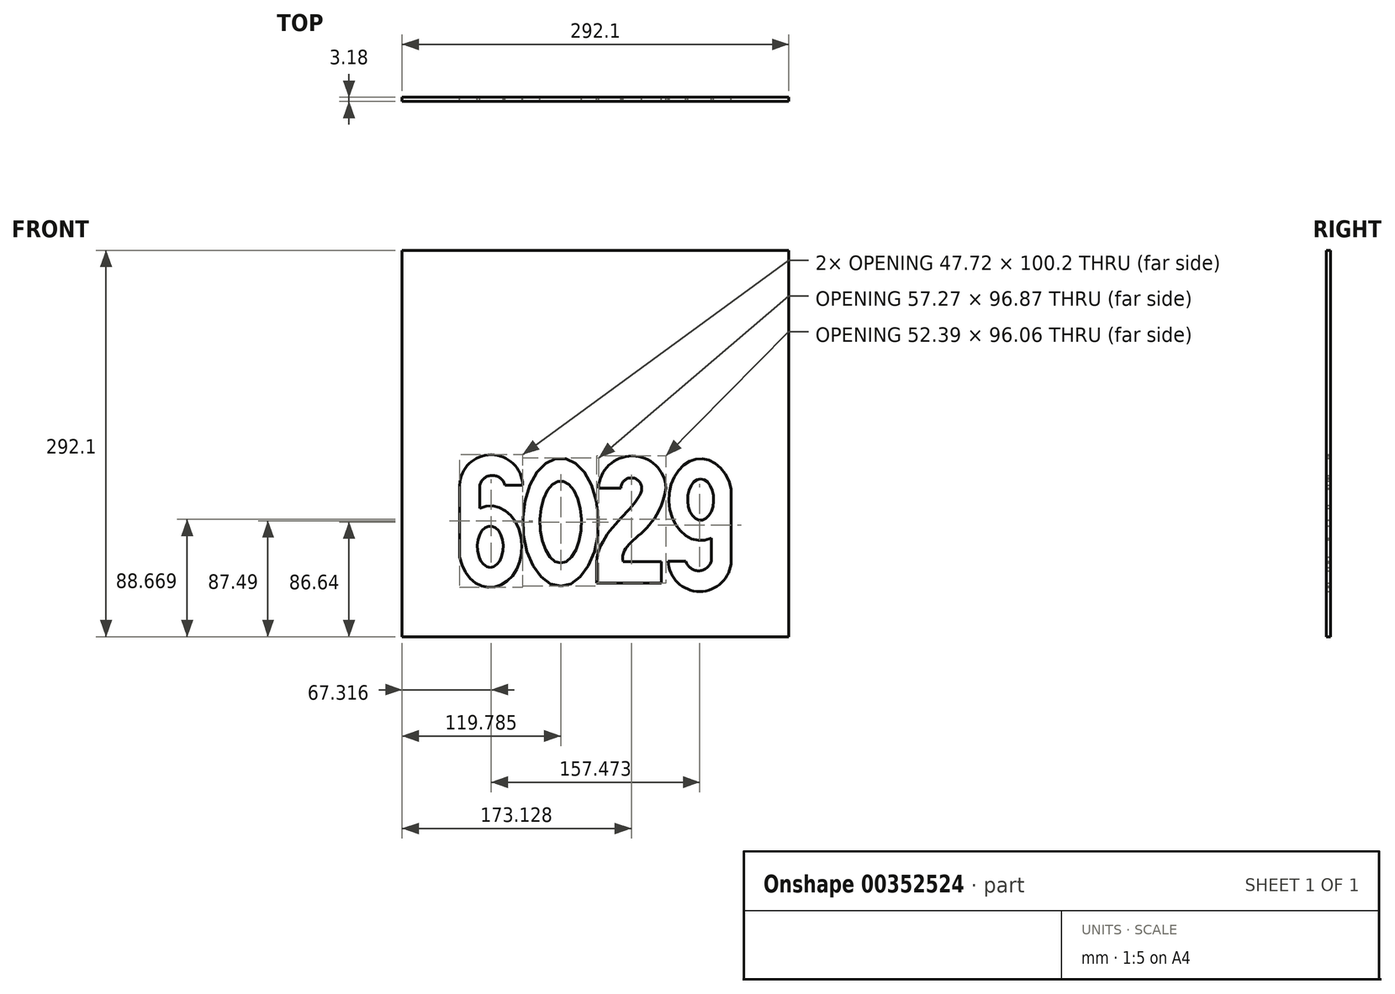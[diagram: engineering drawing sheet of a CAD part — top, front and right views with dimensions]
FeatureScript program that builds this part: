
annotation { "Feature Type Name" : "Feature", "Feature Type Description" : "" }
export const myFeature = defineFeature(function(context is Context, id is Id, definition is map)
    precondition{}
    {
        {
            var Q0;
            Q0=qCreatedBy(makeId("Front.planeOp"),FACE);
            var sketch = newSketch(context, id + "F0", { "sketchPlane" : qUnion([Q0])});
            skLineSegment(sketch, "E0", {"start": v(-95.03, -29.54) * mm, "end": v(-108.48, -29.54) * mm});
            skArc(sketch, "E1", {"start": v(-108.48, -29.54) * mm, "mid": v(-118.05, -22.2) * mm, "end": v(-127.62, -29.54) * mm});
            skArc(sketch, "E2", {"start": v(-95.03, -29.54) * mm, "mid": v(-118.9, -6.52) * mm, "end": v(-142.76, -29.54) * mm});
            skLineSegment(sketch, "E3", {"start": v(-142.76, -29.54) * mm, "end": v(-142.76, -83.99) * mm});
            skLineSegment(sketch, "E4", {"start": v(-127.62, -29.54) * mm, "end": v(-127.62, -46.95) * mm});
            skEllipse(sketch, "E5", {"center": v(-119.6, -76.04) * mm, "majorRadius": 15.63 * mm, "minorRadius": 9.82 * mm, "majorAxis": v(0, -1)});
            skEllipticalArc(sketch, "E6", {});
            skEllipse(sketch, "E7", {"center": v(-66.42, -57.47) * mm, "majorRadius": 48.44 * mm, "minorRadius": 28.64 * mm, "majorAxis": v(0, -1)});
            skEllipse(sketch, "E8", {"center": v(-66.42, -57.47) * mm, "majorRadius": 30.97 * mm, "minorRadius": 15.64 * mm, "majorAxis": v(0, -1)});
            skLineSegment(sketch, "E9", {"start": v(-20.92, -31.85) * mm, "end": v(-37.78, -31.85) * mm});
            skLineSegment(sketch, "E10", {"start": v(9.67, -103.47) * mm, "end": v(-39.28, -103.47) * mm});
            skLineSegment(sketch, "E11", {"start": v(9.67, -103.47) * mm, "end": v(9.67, -87.41) * mm});
            skLineSegment(sketch, "E12", {"start": v(9.67, -87.41) * mm, "end": v(-19.4, -87.41) * mm});
            skArc(sketch, "E13", {"start": v(13.11, -31.85) * mm, "mid": v(-12.34, -7.4) * mm, "end": v(-37.78, -31.85) * mm});
            skFitSpline(sketch, "E14", {"points": [v(13.11, -31.85) * mm, v(-19.4, -87.41) * mm], "startDerivative": vector(-19.5, -113.57) * mm, "endDerivative": vector(9.18, -55.06) * mm});
            skArc(sketch, "E15", {"start": v(-5.24, -31.85) * mm, "mid": v(-13.08, -24.01) * mm, "end": v(-20.92, -31.85) * mm});
            skLineSegment(sketch, "E16", {"start": v(-39.28, -87.41) * mm, "end": v(-39.28, -103.47) * mm});
            skPoint(sketch, "E16.startSnap0", {"position": v(-4.86, -87.41) * mm});
            skFitSpline(sketch, "E17", {"points": [v(-39.28, -87.41) * mm, v(-5.24, -31.85) * mm], "startDerivative": vector(4, 74.7) * mm, "endDerivative": vector(1.15, 42.45) * mm});
            skLineSegment(sketch, "E18", {"start": v(14.72, -86.95) * mm, "end": v(28.17, -86.95) * mm});
            skArc(sketch, "E19", {"start": v(28.17, -86.95) * mm, "mid": v(37.73, -94.28) * mm, "end": v(47.3, -86.95) * mm});
            skArc(sketch, "E20", {"start": v(14.72, -86.95) * mm, "mid": v(38.58, -109.97) * mm, "end": v(62.44, -86.95) * mm});
            skLineSegment(sketch, "E21", {"start": v(62.44, -86.95) * mm, "end": v(62.44, -32.5) * mm});
            skEllipse(sketch, "E22", {"center": v(39.29, -40.45) * mm, "majorRadius": 15.63 * mm, "minorRadius": 9.82 * mm, "majorAxis": v(0, 1)});
            skEllipticalArc(sketch, "E23", {});
            skLineSegment(sketch, "E24", {"start": v(47.3, -86.95) * mm, "end": v(47.3, -69.54) * mm});
            skLineSegment(sketch, "E25.bottom", {"start": v(-186.2, -144.11) * mm, "end": v(105.9, -144.11) * mm});
            skLineSegment(sketch, "E25.top", {"start": v(-186.2, 147.99) * mm, "end": v(105.9, 147.99) * mm});
            skLineSegment(sketch, "E25.left", {"start": v(-186.2, -144.11) * mm, "end": v(-186.2, 147.99) * mm});
            skLineSegment(sketch, "E25.right", {"start": v(105.9, -144.11) * mm, "end": v(105.9, 147.99) * mm});
            const initialGuessF0  = {"E6": [-0.11960215085978274, -0.07604163817507714, 0, -1, 0.030871672671253313, 0.023960798996810216, 4.972696766627012, 3.4826250035732884], "E23": [0.039287207804596644, -0.04044740727788268, 0, 1, 0.030871672671253313, 0.023960798996810216, 4.972696766627028, 3.482625003573289]};
            skSetInitialGuess(sketch, initialGuessF0);
            skSolve(sketch);
        }
        {
            var Q0;
            Q0=makeQuery(id+"F0.imprint","IMPRINT",FACE,{"disambiguationData":[TD([[makeQuery(id+"F0.imprint","IMPRINT",EDGE,{"derivedFrom":sQuery(id+"F0.wireOp",EDGE,"E0")}),1.0]])]});
            var Q1;
            Q1=makeQuery(id+"F0.imprint","IMPRINT",FACE,{"disambiguationData":[TD([[makeQuery(id+"F0.imprint","IMPRINT",EDGE,{"derivedFrom":sQuery(id+"F0.wireOp",EDGE,"E8")}),1.0]])]});
            var Q2;
            Q2=makeQuery(id+"F0.imprint","IMPRINT",FACE,{"disambiguationData":[TD([[makeQuery(id+"F0.imprint","IMPRINT",EDGE,{"derivedFrom":sQuery(id+"F0.wireOp",EDGE,"E5")}),1.0]])]});
            var Q3;
            Q3=makeQuery(id+"F0.imprint","IMPRINT",FACE,{"disambiguationData":[TD([[makeQuery(id+"F0.imprint","IMPRINT",EDGE,{"derivedFrom":sQuery(id+"F0.wireOp",EDGE,"E22")}),1.0]])]});
            extrude(context, id + "F1", {"entities" : qUnion([Q0, Q1, Q2, Q3]), "depth" : 3.17 * mm});
        }
    });
